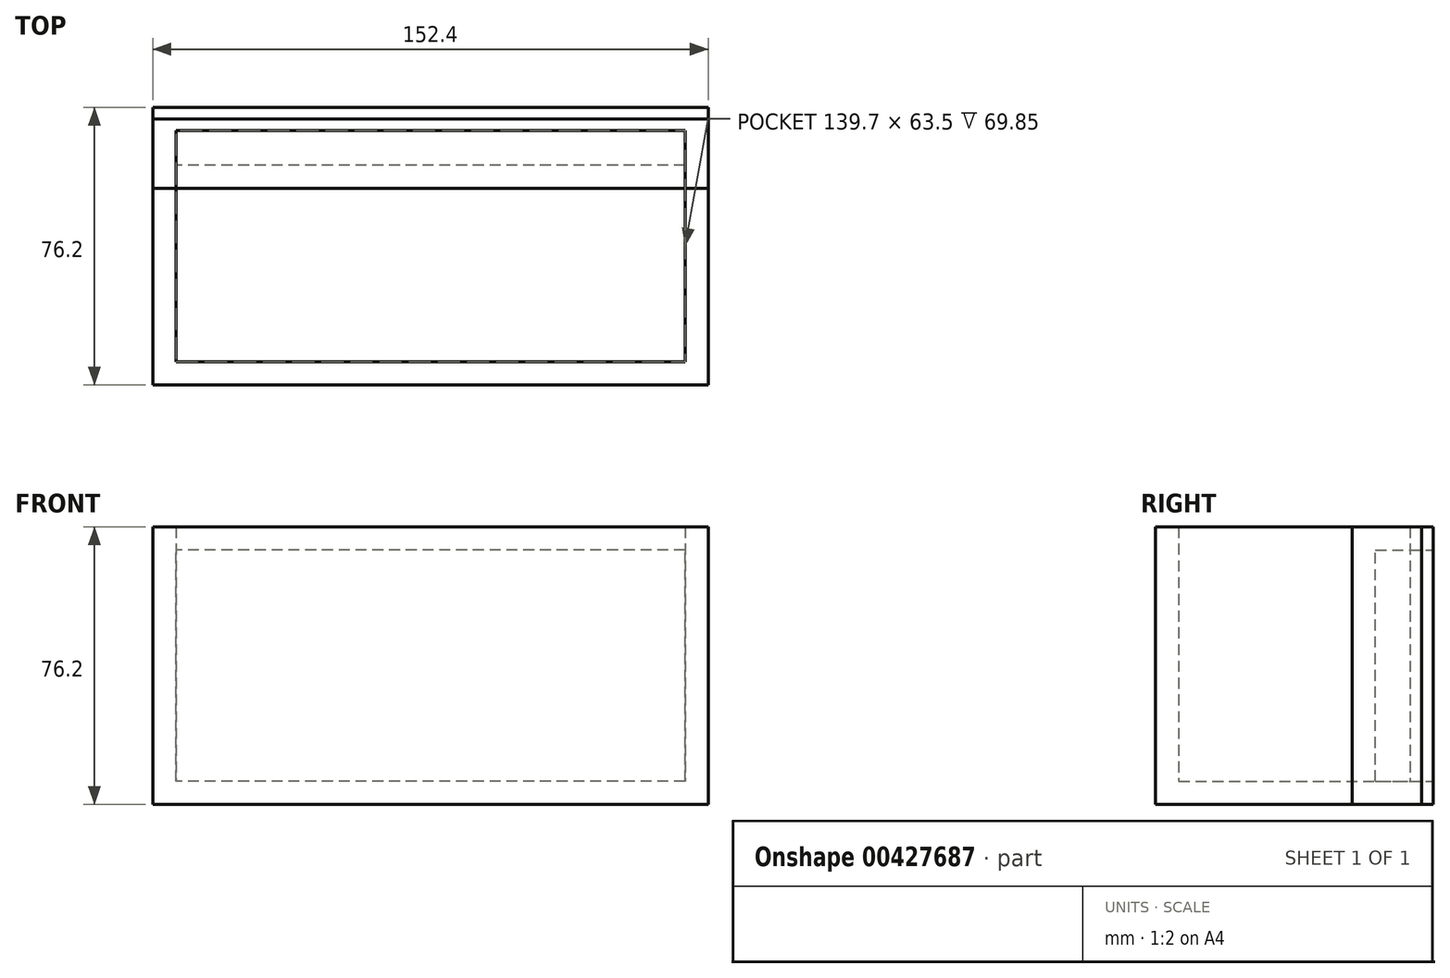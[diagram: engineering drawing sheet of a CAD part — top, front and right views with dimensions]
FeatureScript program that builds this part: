
annotation { "Feature Type Name" : "Feature", "Feature Type Description" : "" }
export const myFeature = defineFeature(function(context is Context, id is Id, definition is map)
    precondition{}
    {
        {
            var Q0;
            Q0=qCreatedBy(makeId("Front.planeOp"),FACE);
            var sketch = newSketch(context, id + "F0", { "sketchPlane" : qUnion([Q0])});
            skLineSegment(sketch, "E0.bottom", {"start": v(76.2, 38.1) * mm, "end": v(-76.2, 38.1) * mm});
            skLineSegment(sketch, "E0.top", {"start": v(76.2, -38.1) * mm, "end": v(-76.2, -38.1) * mm});
            skLineSegment(sketch, "E0.left", {"start": v(76.2, 38.1) * mm, "end": v(76.2, -38.1) * mm});
            skLineSegment(sketch, "E0.right", {"start": v(-76.2, 38.1) * mm, "end": v(-76.2, -38.1) * mm});
            skPoint(sketch, "E0.middle", {"position": v(0, 0) * mm});
            skSolve(sketch);
        }
        {
            var Q0;
            Q0 = qSketchRegion(id + "F0", true);
            extrude(context, id + "F1", {"entities" : qUnion([Q0]), "depth" : 76.2 * mm});
        }
        {
            var Q0;
            Q0=qCreatedBy(makeId("Front.planeOp"),FACE);
            var sketch = newSketch(context, id + "F2", { "sketchPlane" : qUnion([Q0])});
            skLineSegment(sketch, "E1.bottom", {"start": v(76.2, -38.1) * mm, "end": v(-76.2, -38.1) * mm});
            skLineSegment(sketch, "E1.top", {"start": v(76.2, 38.1) * mm, "end": v(-76.2, 38.1) * mm});
            skLineSegment(sketch, "E1.left", {"start": v(76.2, -38.1) * mm, "end": v(76.2, 38.1) * mm});
            skLineSegment(sketch, "E1.right", {"start": v(-76.2, -38.1) * mm, "end": v(-76.2, 38.1) * mm});
            skPoint(sketch, "E1.middle", {"position": v(0, 0) * mm});
            skSolve(sketch);
        }
        {
            var Q0;
            Q0 = qSketchRegion(id + "F2", true);
            extrude(context, id + "F3", {"entities" : qUnion([Q0]), "depth" : 22.22 * mm});
        }
        {
            var Q0;
            Q0=makeQuery(id+"F1.opExtrude","SWEPT_FACE",FACE,{"disambiguationData":[OSD([sQuery(id+"F0.wireOp",EDGE,"E0.bottom")])]});
            var Q1;
            Q1=makeQuery(id+"F1.opExtrude","SWEPT_BODY",BODY,{"disambiguationData":[OSD([sQuery(id+"F0.wireOp",EDGE,"E0.bottom"),sQuery(id+"F0.wireOp",EDGE,"E0.top"),sQuery(id+"F0.wireOp",EDGE,"E0.left"),sQuery(id+"F0.wireOp",EDGE,"E0.right")])]});
            shell(context, id + "F4", {"entities" : qUnion([Q0]), "parts" : qUnion([Q1]), "thickness" : 6.35 * mm});
        }
        {
            var Q0;
            Q0=makeQuery(id+"F3.opExtrude","CAP_FACE",FACE,{"disambiguationData":[OSD([sQuery(id+"F2.wireOp",EDGE,"E1.bottom"),sQuery(id+"F2.wireOp",EDGE,"E1.top"),sQuery(id+"F2.wireOp",EDGE,"E1.left"),sQuery(id+"F2.wireOp",EDGE,"E1.right")])],"isStart":true});
            var Q1;
            Q1=makeQuery(id+"F3.opExtrude","SWEPT_BODY",BODY,{"disambiguationData":[OSD([sQuery(id+"F2.wireOp",EDGE,"E1.bottom"),sQuery(id+"F2.wireOp",EDGE,"E1.top"),sQuery(id+"F2.wireOp",EDGE,"E1.left"),sQuery(id+"F2.wireOp",EDGE,"E1.right")])]});
            shell(context, id + "F5", {"entities" : qUnion([Q0]), "parts" : qUnion([Q1]), "thickness" : 6.35 * mm});
        }
        {
            var Q0;
            Q0 = qSketchRegion(id + "F0", true);
            extrude(context, id + "F6", {"entities" : qUnion([Q0]), "depth" : 3.17 * mm});
        }
    });
